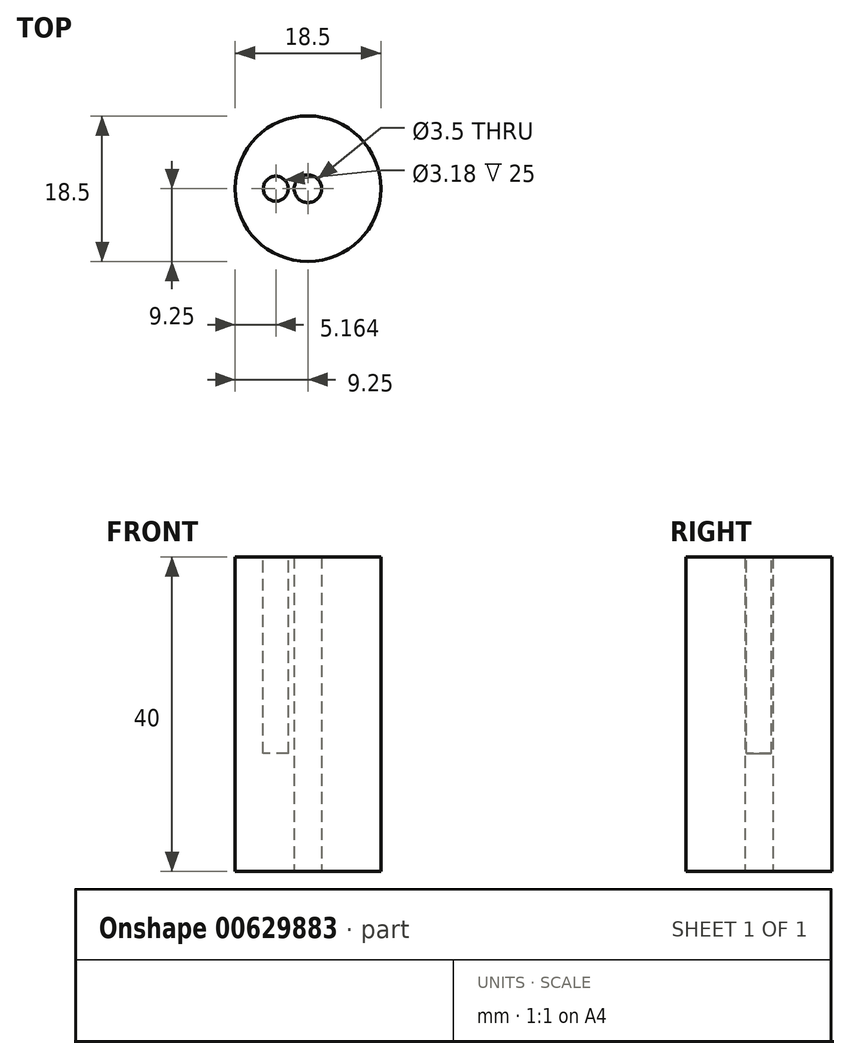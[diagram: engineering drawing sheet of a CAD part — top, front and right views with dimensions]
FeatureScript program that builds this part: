
annotation { "Feature Type Name" : "Feature", "Feature Type Description" : "" }
export const myFeature = defineFeature(function(context is Context, id is Id, definition is map)
    precondition{}
    {
        {
            var Q0;
            Q0=qCreatedBy(makeId("Top.planeOp"),FACE);
            var sketch = newSketch(context, id + "F0", { "sketchPlane" : qUnion([Q0])});
            skCircle(sketch, "E0", {"center": v(0, 0) * mm, "radius": 9.25 * mm});
            skLineSegment(sketch, "E1", {"start": v(5.6, 3.4) * mm, "end": v(5.6, -3.23) * mm, "construction": true});
            skCircle(sketch, "E2", {"center": v(0, 0) * mm, "radius": 1.75 * mm});
            skSolve(sketch);
        }
        {
            var Q0;
            Q0=makeQuery(id+"F0.imprint","IMPRINT",FACE,{"disambiguationData":[TD([[makeQuery(id+"F0.imprint","IMPRINT",EDGE,{"derivedFrom":sQuery(id+"F0.wireOp",EDGE,"E0")}),1.0]])]});
            extrude(context, id + "F1", {"entities" : qUnion([Q0]), "depth" : 25 * mm, "offsetDistance" : 25 * mm});
        }
        {
            var Q0;
            Q0=makeQuery(id+"F1.opExtrude","CAP_FACE",FACE,{"disambiguationData":[OSD([sQuery(id+"F0.wireOp",EDGE,"E0"),sQuery(id+"F0.wireOp",EDGE,"otiNSaUE-70pt-2M1a-yiYi-CeAqDzbHh0Mo"),sQuery(id+"F0.wireOp",EDGE,"E2")])],"isStart":true});
            extrude(context, id + "F2", {"entities" : qUnion([Q0]), "operationType" : NewBodyOperationType.ADD, "depth" : 15 * mm, "offsetDistance" : 25 * mm});
        }
        {
            var Q0;
            Q0=makeQuery(id+"F1.opExtrude","CAP_FACE",FACE,{"disambiguationData":[OSD([sQuery(id+"F0.wireOp",EDGE,"E0"),sQuery(id+"F0.wireOp",EDGE,"otiNSaUE-70pt-2M1a-yiYi-CeAqDzbHh0Mo"),sQuery(id+"F0.wireOp",EDGE,"E2")])],"isStart":false});
            var sketch = newSketch(context, id + "F3", { "sketchPlane" : qUnion([Q0])});
            skLineSegment(sketch, "E3", {"start": v(-4.09, 0) * mm, "end": v(-4.09, 4.35) * mm, "construction": true});
            skSolve(sketch);
        }
        {
            var Q0;
            Q0=makeQuery(id+"F3.imprint","IMPRINT",FACE,{"disambiguationData":[TD([[makeQuery(id+"F3.imprint","IMPRINT",EDGE,{"derivedFrom":makeQuery(id+"F1.opExtrude","CAP_EDGE",EDGE,{"disambiguationData":[OSD([sQuery(id+"F0.wireOp",EDGE,"E0")])],"isStart":false})}),1.0]])]});
            var sketch = newSketch(context, id + "F4", { "sketchPlane" : qUnion([Q0])});
            skCircle(sketch, "E4", {"center": v(-4.09, 0) * mm, "radius": 1.59 * mm});
            skSolve(sketch);
        }
        {
            var Q0;
            Q0 = qSketchRegion(id + "F4", true);
            extrude(context, id + "F5", {"entities" : qUnion([Q0]), "operationType" : NewBodyOperationType.REMOVE, "oppositeDirection" : true, "depth" : 25 * mm, "offsetDistance" : 25 * mm});
        }
    });
